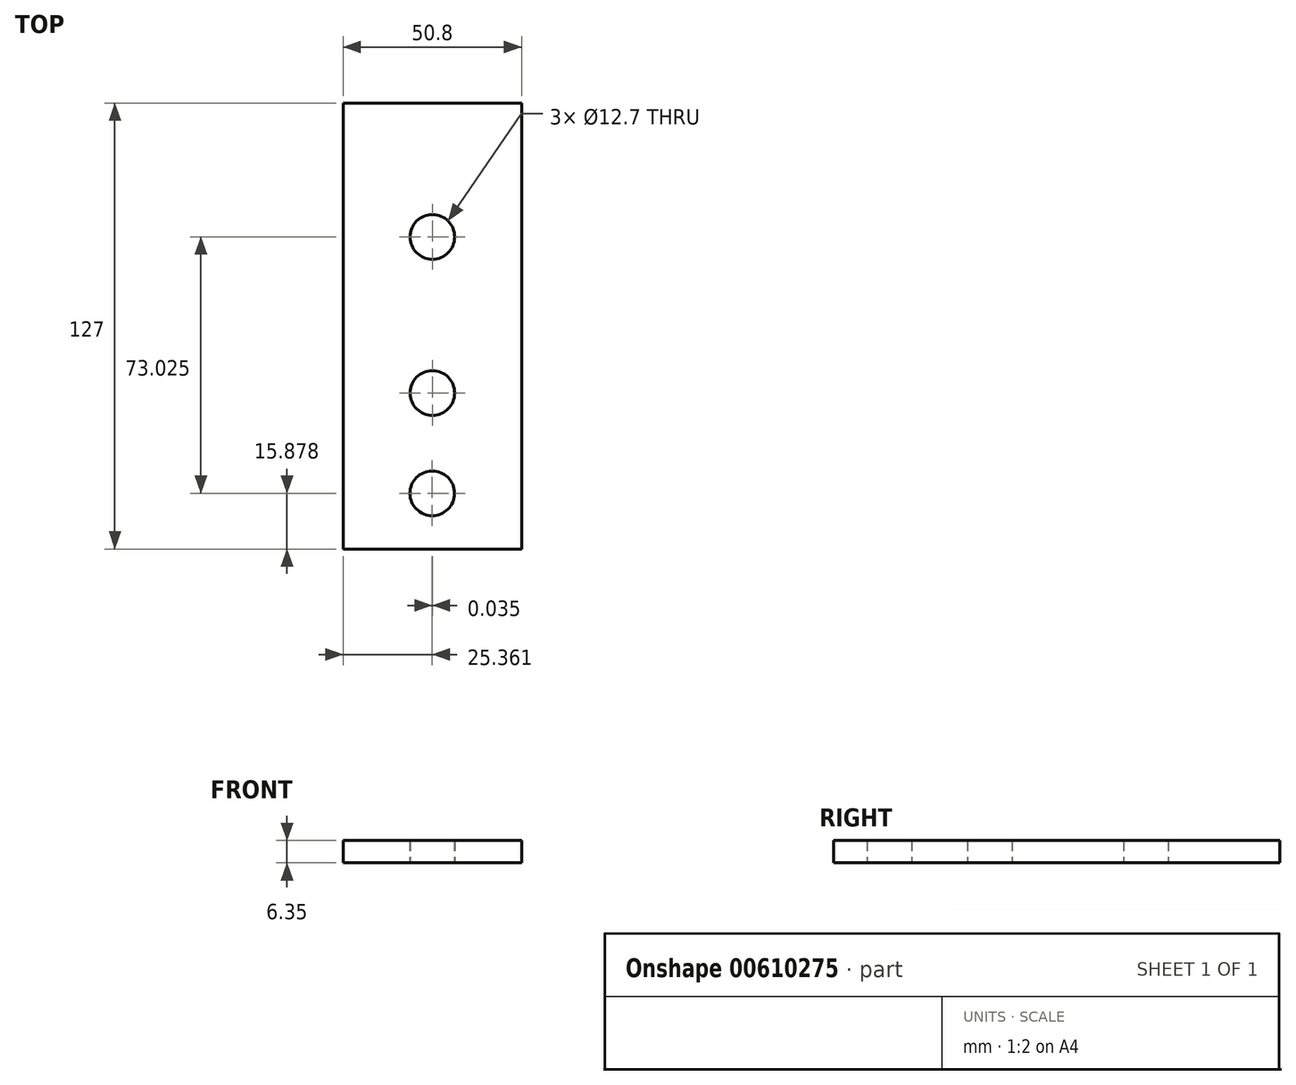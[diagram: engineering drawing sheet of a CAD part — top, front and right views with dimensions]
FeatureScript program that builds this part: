
annotation { "Feature Type Name" : "Feature", "Feature Type Description" : "" }
export const myFeature = defineFeature(function(context is Context, id is Id, definition is map)
    precondition{}
    {
        {
            var Q0;
            Q0=qCreatedBy(makeId("Top.planeOp"),FACE);
            var sketch = newSketch(context, id + "F0", { "sketchPlane" : qUnion([Q0])});
            skLineSegment(sketch, "E0.bottom", {"start": v(-30.48, 94.55) * mm, "end": v(20.32, 94.55) * mm});
            skLineSegment(sketch, "E0.top", {"start": v(-30.48, -32.45) * mm, "end": v(20.32, -32.45) * mm});
            skLineSegment(sketch, "E0.left", {"start": v(-30.48, 94.55) * mm, "end": v(-30.48, -32.45) * mm});
            skLineSegment(sketch, "E0.right", {"start": v(20.32, 94.55) * mm, "end": v(20.32, -32.45) * mm});
            skCircle(sketch, "E1", {"center": v(-5.08, 56.45) * mm, "radius": 6.35 * mm});
            skCircle(sketch, "E2", {"center": v(-5.08, 12) * mm, "radius": 6.35 * mm});
            skCircle(sketch, "E3", {"center": v(-5.12, -16.57) * mm, "radius": 6.35 * mm});
            skLineSegment(sketch, "E4.bottom", {"start": v(-226.01, -11.43) * mm, "end": v(-226.01, 39.37) * mm});
            skLineSegment(sketch, "E4.top", {"start": v(-99.01, -11.43) * mm, "end": v(-99.01, 39.37) * mm});
            skLineSegment(sketch, "E4.left", {"start": v(-226.01, -11.43) * mm, "end": v(-99.01, -11.43) * mm});
            skLineSegment(sketch, "E4.right", {"start": v(-226.01, 39.37) * mm, "end": v(-99.01, 39.37) * mm});
            skCircle(sketch, "E5", {"center": v(-187.91, 1.27) * mm, "radius": 6.35 * mm});
            skCircle(sketch, "E6", {"center": v(-143.46, 1.27) * mm, "radius": 6.35 * mm});
            skCircle(sketch, "E7", {"center": v(-114.89, 1.23) * mm, "radius": 6.35 * mm});
            skSolve(sketch);
        }
        {
            var Q0;
            Q0=makeQuery(id+"F0.imprint","IMPRINT",FACE,{"disambiguationData":[TD([[makeQuery(id+"F0.imprint","IMPRINT",EDGE,{"derivedFrom":sQuery(id+"F0.wireOp",EDGE,"E0.bottom")}),-1.0]])]});
            extrude(context, id + "F1", {"entities" : qUnion([Q0]), "depth" : 6.35 * mm, "offsetDistance" : 25.4 * mm});
        }
    });
